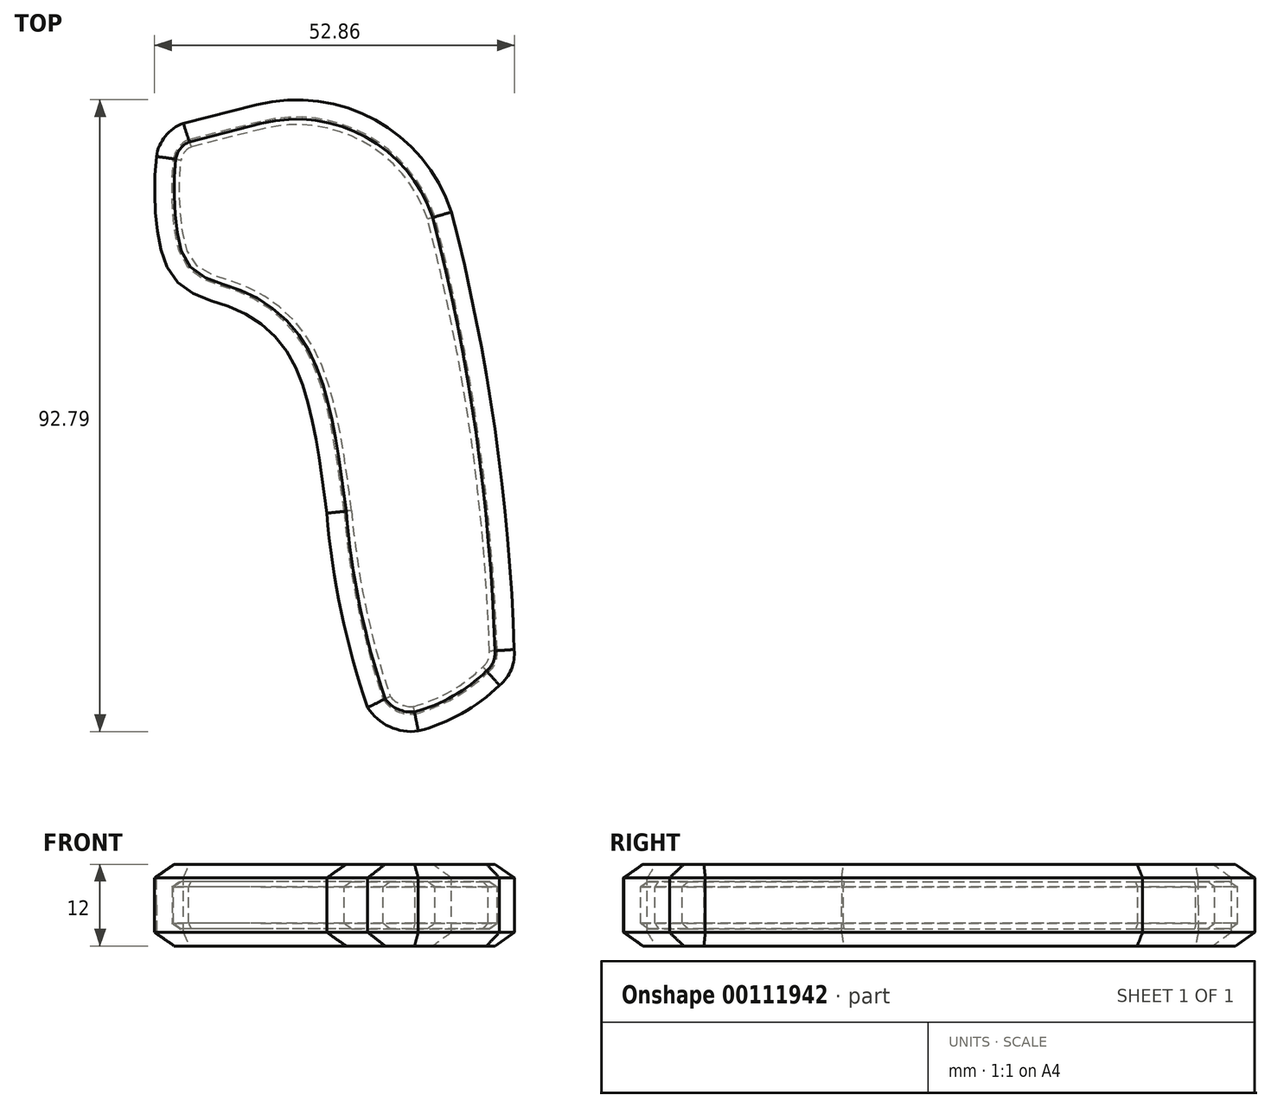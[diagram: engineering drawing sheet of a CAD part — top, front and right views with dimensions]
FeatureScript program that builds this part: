
annotation { "Feature Type Name" : "Feature", "Feature Type Description" : "" }
export const myFeature = defineFeature(function(context is Context, id is Id, definition is map)
    precondition{}
    {
        {
            var Q0;
            Q0=qCreatedBy(makeId("Top.planeOp"),FACE);
            var sketch = newSketch(context, id + "F0", { "sketchPlane" : qUnion([Q0])});
            skPoint(sketch, "E0", {"position": v(-31.69, 34.1) * mm});
            skPoint(sketch, "E1", {"position": v(-29.68, 36.64) * mm});
            skArc(sketch, "E2", {"start": v(-29.68, 36.64) * mm, "mid": v(-31.01, 35.62) * mm, "end": v(-31.69, 34.1) * mm});
            skLineSegment(sketch, "E3", {"start": v(-29.68, 36.64) * mm, "end": v(-19.1, 39.32) * mm});
            skArc(sketch, "E4", {"start": v(6.09, 25.52) * mm, "mid": v(-3.8, 37.37) * mm, "end": v(-19.1, 39.32) * mm});
            skArc(sketch, "E5", {"start": v(15.2, -38.13) * mm, "mid": v(12.4, -6.05) * mm, "end": v(6.09, 25.52) * mm});
            skArc(sketch, "E6", {"start": v(14, -41.06) * mm, "mid": v(14.98, -39.75) * mm, "end": v(15.2, -38.13) * mm});
            skArc(sketch, "E7", {"start": v(3.4, -47.09) * mm, "mid": v(9.08, -44.75) * mm, "end": v(14, -41.06) * mm});
            skPoint(sketch, "E8", {"position": v(-0.9, -45.16) * mm});
            skArc(sketch, "E9", {"start": v(-0.9, -45.16) * mm, "mid": v(1, -46.7) * mm, "end": v(3.4, -47.09) * mm});
            skArc(sketch, "E10", {"start": v(-6.64, -17.6) * mm, "mid": v(-4.61, -31.56) * mm, "end": v(-0.9, -45.16) * mm});
            skPoint(sketch, "E11", {"position": v(-21.1, 14.4) * mm});
            skPoint(sketch, "E12", {"position": v(-12.38, 6.43) * mm});
            skPoint(sketch, "E13", {"position": v(-26.85, 16.46) * mm});
            skPoint(sketch, "E14", {"position": v(-30.6, 19.98) * mm});
            skPoint(sketch, "E15", {"position": v(-31.9, 31.23) * mm});
            skFitSpline(sketch, "E16", {"points": [v(-6.64, -17.6) * mm, v(-12.38, 6.43) * mm, v(-21.1, 14.4) * mm, v(-26.85, 16.46) * mm, v(-30.6, 19.98) * mm, v(-31.9, 31.23) * mm, v(-31.69, 34.1) * mm], "startDerivative": vector(-12.9, 99.78) * mm, "endDerivative": vector(2.83, 23.45) * mm});
            skSolve(sketch);
        }
        {
            var Q0;
            Q0=makeQuery(id+"F0.imprint","IMPRINT",FACE,{"disambiguationData":[TD([[makeQuery(id+"F0.imprint","IMPRINT",EDGE,{"derivedFrom":sQuery(id+"F0.wireOp",EDGE,"E2")}),1.0]])]});
            extrude(context, id + "F1", {"entities" : qUnion([Q0]), "oppositeDirection" : true, "depth" : 2 * mm, "hasDraft" : true, "draftAngle" : 55 * degree});
        }
        {
            var Q0;
            Q0=makeQuery(id+"F1.opExtrude","CAP_FACE",FACE,{"disambiguationData":[OSD([sQuery(id+"F0.wireOp",EDGE,"E2"),sQuery(id+"F0.wireOp",EDGE,"E3"),sQuery(id+"F0.wireOp",EDGE,"E4"),sQuery(id+"F0.wireOp",EDGE,"E5"),sQuery(id+"F0.wireOp",EDGE,"E6"),sQuery(id+"F0.wireOp",EDGE,"E7"),sQuery(id+"F0.wireOp",EDGE,"E9"),sQuery(id+"F0.wireOp",EDGE,"E10"),sQuery(id+"F0.wireOp",EDGE,"E16")])],"isStart":false});
            extrude(context, id + "F2", {"entities" : qUnion([Q0]), "operationType" : NewBodyOperationType.ADD, "depth" : 4 * mm});
        }
        {
            var Q0;
            Q0=makeQuery(id+"F2.opExtrude","CAP_FACE",FACE,{"disambiguationData":[OSD([sQuery(id+"F0.wireOp",EDGE,"E2"),sQuery(id+"F0.wireOp",EDGE,"E3"),sQuery(id+"F0.wireOp",EDGE,"E4"),sQuery(id+"F0.wireOp",EDGE,"E5"),sQuery(id+"F0.wireOp",EDGE,"E6"),sQuery(id+"F0.wireOp",EDGE,"E7"),sQuery(id+"F0.wireOp",EDGE,"E9"),sQuery(id+"F0.wireOp",EDGE,"E10"),sQuery(id+"F0.wireOp",EDGE,"E16")])],"isStart":false});
            shell(context, id + "F3", {"entities" : qUnion([Q0]), "thickness" : 2.54 * mm});
        }
        {
            var Q0;
            Q0=makeQuery(id+"F1.opExtrude","SWEPT_BODY",BODY,{"disambiguationData":[OSD([sQuery(id+"F0.wireOp",EDGE,"E2"),sQuery(id+"F0.wireOp",EDGE,"E3"),sQuery(id+"F0.wireOp",EDGE,"E4"),sQuery(id+"F0.wireOp",EDGE,"E5"),sQuery(id+"F0.wireOp",EDGE,"E6"),sQuery(id+"F0.wireOp",EDGE,"E7"),sQuery(id+"F0.wireOp",EDGE,"E9"),sQuery(id+"F0.wireOp",EDGE,"E10"),sQuery(id+"F0.wireOp",EDGE,"E16")])]});
            var Q1;
            Q1=makeQuery(id+"F2.opExtrude","CAP_FACE",FACE,{"disambiguationData":[OSD([sQuery(id+"F0.wireOp",EDGE,"E2"),sQuery(id+"F0.wireOp",EDGE,"E3"),sQuery(id+"F0.wireOp",EDGE,"E4"),sQuery(id+"F0.wireOp",EDGE,"E5"),sQuery(id+"F0.wireOp",EDGE,"E6"),sQuery(id+"F0.wireOp",EDGE,"E7"),sQuery(id+"F0.wireOp",EDGE,"E9"),sQuery(id+"F0.wireOp",EDGE,"E10"),sQuery(id+"F0.wireOp",EDGE,"E16")])],"isStart":false});
            mirror(context, id + "F4", {"operationType" : NewBodyOperationType.ADD, "entities" : qUnion([Q0]), "mirrorPlane" : qUnion([Q1])});
        }
    });
